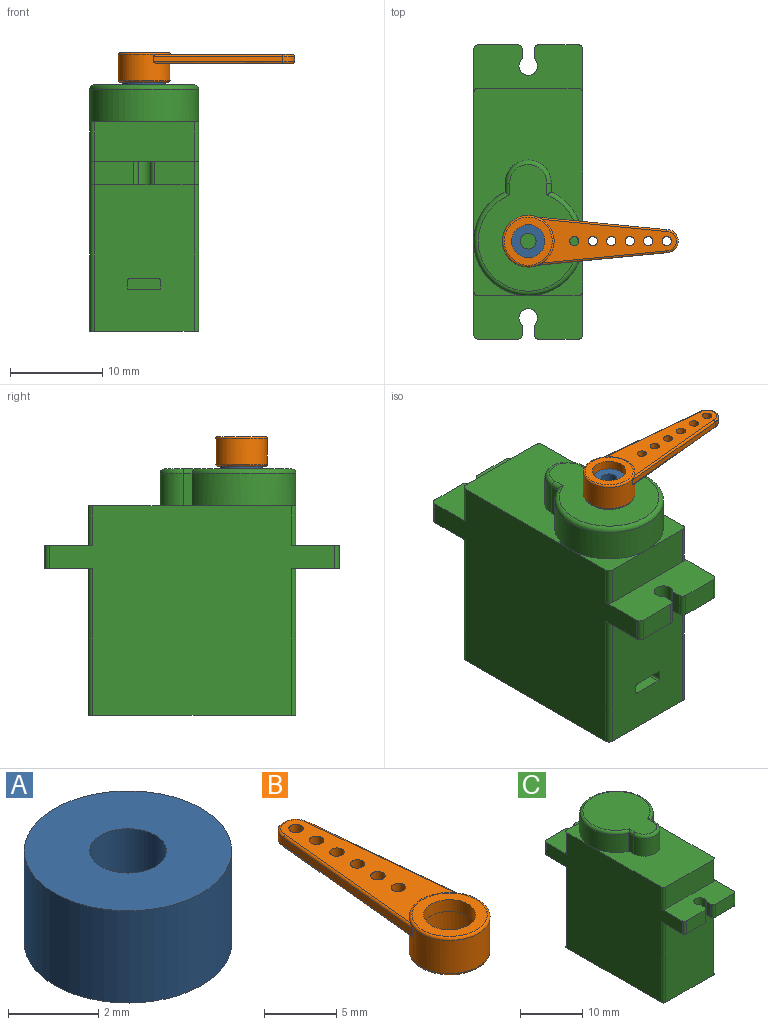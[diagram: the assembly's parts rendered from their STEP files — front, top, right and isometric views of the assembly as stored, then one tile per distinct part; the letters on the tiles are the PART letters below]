
ASSEMBLY  parts=3 mates=2
PART A: 4 faces, bbox 4.6x4.6x2.5 mm
  f0: cylinder r=0.85mm len=2.5mm, axis (0,0,-1), area 13.4mm2, adj f2,f3
  f1: cylinder r=2.3mm len=4.6mm, axis (0,0,-1), area 36.1mm2, adj f2,f3
  f2: plane 4.6x4.6mm, normal (0,0,1), area 14.3mm2, adj f0,f1
  f3: plane 4.6x4.6mm, normal (0,0,-1), area 14.3mm2, adj f0,f1
PART B: 25 faces, bbox 6.1x19.4x3.2 mm
  f0: cylinder r=2.3mm len=4.6mm, axis (0,0,1), area 31.8mm2, adj f2,f5
  f1: cylinder r=2.8mm len=5.6mm, axis (0,0,1), area 42.6mm2, adj f6,f8,f15,f17,f18,f20,f21,f23
  f2: plane 5.2x5.2mm, normal (0,0,-1), area 4.6mm2, adj f0,f24
  f3: plane 5.2x5.2mm, normal (0,0,1), area 11.1mm2, adj f4,f17
  f4: cylinder r=1.8mm len=3.6mm, axis (0,0,-1), area 11.3mm2, adj f3,f5
  f5: plane 4.6x4.6mm, normal (0,0,-1), area 6.4mm2, adj f0,f4
  f6: plane 13.99x1.36mm, normal (1,0.1,0), area 8.4mm2, adj f1,f7,f18,f21
  f7: cylinder r=1.25mm len=2.5mm, axis (0,0,1), area 2.4mm2, adj f6,f8,f19,f22
  f8: plane 13.99x1.36mm, normal (-1,0.1,0), area 8.4mm2, adj f1,f7,f20,f23
  f9: cylinder r=0.5mm len=1mm, axis (0,0,1), area 3.1mm2, adj f15,f16
  f10: cylinder r=0.5mm len=1mm, axis (0,0,1), area 3.1mm2, adj f15,f16
  f11: cylinder r=0.5mm len=1mm, axis (0,0,1), area 3.1mm2, adj f15,f16
  f12: cylinder r=0.5mm len=1mm, axis (0,0,1), area 3.1mm2, adj f15,f16
  f13: cylinder r=0.5mm len=1mm, axis (0,0,1), area 3.1mm2, adj f15,f16
  f14: cylinder r=0.5mm len=1mm, axis (0,0,1), area 3.1mm2, adj f15,f16
  f15: plane 14.55x4.73mm, normal (0,0,-1), area 38.7mm2, adj f1,f9,f10,f11,f12,f13,f14,f21
  f16: plane 14.55x4.73mm, normal (0,0,1), area 38.7mm2, adj f9,f10,f11,f12,f13,f14,f17,f18
  f17: torus R=2.6mm, axis (0,0,1), area 5.4mm2, adj f1,f3,f16
  f18: cylinder r=0.2mm len=14.02mm, axis (-0.1,1,0), area 4.3mm2, adj f1,f6,f16,f19
  f19: torus R=1.05mm, axis (0,0,1), area 1.2mm2, adj f7,f16,f18,f20
  f20: cylinder r=0.2mm len=14.02mm, axis (-0.1,-1,0), area 4.3mm2, adj f1,f8,f16,f19
  f21: cylinder r=0.2mm len=14.02mm, axis (0.1,-1,0), area 4.3mm2, adj f1,f6,f15,f22
  f22: torus R=1.05mm, axis (0,0,1), area 1.2mm2, adj f7,f15,f21,f23
  f23: cylinder r=0.2mm len=14.02mm, axis (0.1,1,0), area 4.3mm2, adj f1,f8,f15,f22
  f24: torus R=2.6mm, axis (0,0,1), area 5.4mm2, adj f1,f2
PART C: 58 faces, bbox 12.8x31.9x26.7 mm
  f0: plane 16.6x11.8mm, normal (0,0,1), area 128.4mm2, adj f12,f16,f17,f24,f25,f26,f27,f29
  f1: plane 5.9x5.9mm, normal (0,0,1), area 7.4mm2, adj f11,f16,f24,f34
  f2: plane 5.9x5.9mm, normal (0,0,1), area 7.4mm2, adj f11,f17,f24,f30
  f3: plane 4.25x2.5mm, normal (0,1,0), area 10.6mm2, adj f5,f6,f38,f44
  f4: plane 4.25x2.5mm, normal (0,-1,0), area 10.6mm2, adj f7,f8,f40,f43
  f5: plane 11.8x5.2mm, normal (0,0,-1), area 50.4mm2, adj f3,f9,f10,f16,f17,f21,f22,f23
  f6: plane 11.8x5.2mm, normal (0,0,1), area 50.4mm2, adj f3,f10,f11,f16,f17,f21,f22,f23
  f7: plane 11.8x5.2mm, normal (0,0,1), area 50.4mm2, adj f4,f12,f13,f16,f17,f18,f19,f20
  f8: plane 11.8x5.2mm, normal (0,0,-1), area 50.4mm2, adj f4,f13,f14,f16,f17,f18,f19,f20
  f9: plane 15.9x10.8mm, normal (0,1,0), area 167.4mm2, adj f5,f15,f32,f36,f49,f50,f51,f52
  f10: plane 4.25x2.5mm, normal (0,1,0), area 10.6mm2, adj f5,f6,f37,f42
  f11: plane 10.8x4.3mm, normal (0,1,0), area 46.4mm2, adj f1,f2,f6,f30,f34
  f12: plane 10.8x4.3mm, normal (0,-1,0), area 46.4mm2, adj f0,f7,f29,f33
  f13: plane 4.25x2.5mm, normal (0,-1,0), area 10.6mm2, adj f7,f8,f39,f41
  f14: plane 15.9x10.8mm, normal (0,-1,0), area 171.7mm2, adj f8,f15,f31,f35
  f15: plane 22.5x11.8mm, normal (0,0,-1), area 265.3mm2, adj f9,f14,f16,f17,f31,f32,f35,f36
  f16: plane 30.9x22.7mm, normal (1,0,0), area 511.6mm2, adj f0,f1,f5,f6,f7,f8,f15,f33
  f17: plane 30.9x22.7mm, normal (-1,0,0), area 511.5mm2, adj f0,f2,f5,f6,f7,f8,f15,f29
  f18: plane 2.5x1.04mm, normal (-1,0,0), area 2.6mm2, adj f7,f8,f20,f40
  f19: plane 2.5x1.04mm, normal (1,0,0), area 2.6mm2, adj f7,f8,f20,f39
  f20: cylinder r=1mm len=2.5mm, axis (0,0,1), area 12.2mm2, adj f7,f8,f18,f19
  f21: plane 2.5x1.04mm, normal (1,0,0), area 2.6mm2, adj f5,f6,f22,f37
  f22: cylinder r=1mm len=2.5mm, axis (0,0,1), area 12.2mm2, adj f5,f6,f21,f23
  f23: plane 2.5x1.04mm, normal (-1,0,0), area 2.6mm2, adj f5,f6,f22,f38
  f24: cylinder r=5.9mm len=11.8mm, axis (0,0,-1), area 111.7mm2, adj f0,f1,f2,f25,f27,f47
  f25: plane 3.5x0.96mm, normal (-1,0,0), area 3.3mm2, adj f0,f24,f26,f45
  f26: cylinder r=2.5mm len=5mm, axis (0,0,-1), area 27.5mm2, adj f0,f25,f27,f46
  f27: plane 3.5x0.96mm, normal (1,0,0), area 3.3mm2, adj f0,f24,f26,f48
  f28: plane 13.7x10.8mm, normal (0,0,1), area 102mm2, adj f45,f46,f47,f48
  f29: cylinder r=0.5mm len=4.3mm, axis (0,0,-1), area 3.4mm2, adj f0,f7,f12,f17
  f30: cylinder r=0.5mm len=4.3mm, axis (0,0,1), area 3.4mm2, adj f2,f6,f11,f17
  f31: cylinder r=0.5mm len=15.9mm, axis (0,0,-1), area 12.5mm2, adj f8,f14,f15,f17
  f32: cylinder r=0.5mm len=15.9mm, axis (0,0,1), area 12.5mm2, adj f5,f9,f15,f17
  f33: cylinder r=0.5mm len=4.3mm, axis (0,0,1), area 3.4mm2, adj f0,f7,f12,f16
  f34: cylinder r=0.5mm len=4.3mm, axis (0,0,-1), area 3.4mm2, adj f1,f6,f11,f16
  f35: cylinder r=0.5mm len=15.9mm, axis (0,0,1), area 12.5mm2, adj f8,f14,f15,f16
  f36: cylinder r=0.5mm len=15.9mm, axis (0,0,-1), area 12.5mm2, adj f5,f9,f15,f16
  f37: cylinder r=0.5mm len=2.5mm, axis (0,0,-1), area 2mm2, adj f5,f6,f10,f21
  f38: cylinder r=0.5mm len=2.5mm, axis (0,0,1), area 2mm2, adj f3,f5,f6,f23
  f39: cylinder r=0.5mm len=2.5mm, axis (0,0,-1), area 2mm2, adj f7,f8,f13,f19
  f40: cylinder r=0.5mm len=2.5mm, axis (0,0,1), area 2mm2, adj f4,f7,f8,f18
  f41: cylinder r=0.5mm len=2.5mm, axis (0,0,-1), area 2mm2, adj f7,f8,f13,f17
  f42: cylinder r=0.5mm len=2.5mm, axis (0,0,1), area 2mm2, adj f5,f6,f10,f17
  f43: cylinder r=0.5mm len=2.5mm, axis (0,0,1), area 2mm2, adj f4,f7,f8,f16
  f44: cylinder r=0.5mm len=2.5mm, axis (0,0,-1), area 2mm2, adj f3,f5,f6,f16
  f45: cylinder r=0.5mm len=1.28mm, axis (0,1,0), area 0.8mm2, adj f25,f28,f46,f47
  f46: torus R=2mm, axis (0,0,1), area 5.7mm2, adj f26,f28,f45,f48
  f47: torus R=5.4mm, axis (0,0,1), area 24.5mm2, adj f24,f28,f45,f48
  f48: cylinder r=0.5mm len=1.28mm, axis (0,-1,0), area 0.8mm2, adj f27,f28,f46,f47
  f49: plane 1.5x0.8mm, normal (1,0,0), area 1.2mm2, adj f9,f53,f54,f57
  f50: plane 3.2x1.5mm, normal (0,0,-1), area 4.8mm2, adj f9,f53,f54,f55
  f51: plane 1.5x0.8mm, normal (-1,0,0), area 1.2mm2, adj f9,f53,f55,f56
  f52: plane 3.2x1.5mm, normal (0,0,1), area 4.8mm2, adj f9,f53,f56,f57
  f53: plane 3.6x1.2mm, normal (0,1,0), area 4.3mm2, adj f49,f50,f51,f52,f54,f55,f56,f57
  f54: cylinder r=0.2mm len=1.5mm, axis (0,-1,0), area 0.5mm2, adj f9,f49,f50,f53
  f55: cylinder r=0.2mm len=1.5mm, axis (0,1,0), area 0.5mm2, adj f9,f50,f51,f53
  f56: cylinder r=0.2mm len=1.5mm, axis (0,-1,0), area 0.5mm2, adj f9,f51,f52,f53
  f57: cylinder r=0.2mm len=1.5mm, axis (0,1,0), area 0.5mm2, adj f9,f49,f52,f53
PLACE A rot(axis=(0,0,-1),90deg) t=(-5.41,-18.99,-16.7)mm
PLACE B rot(axis=(0,0,-1),90deg) t=(-5.41,-18.99,-16.7)mm
PLACE C rot(axis=(0,0,1),180deg) t=(-0.06,-13.64,-16.7)mm fixed
MATE fastened B.f0 <-> A.f0  axis (0,0,-1) through (-0.06,-18.99,1.15)mm
MATE revolute A.f0 <-> C.f24  axis (0,0,-1) through (-0.06,-18.99,-1.35)mm
